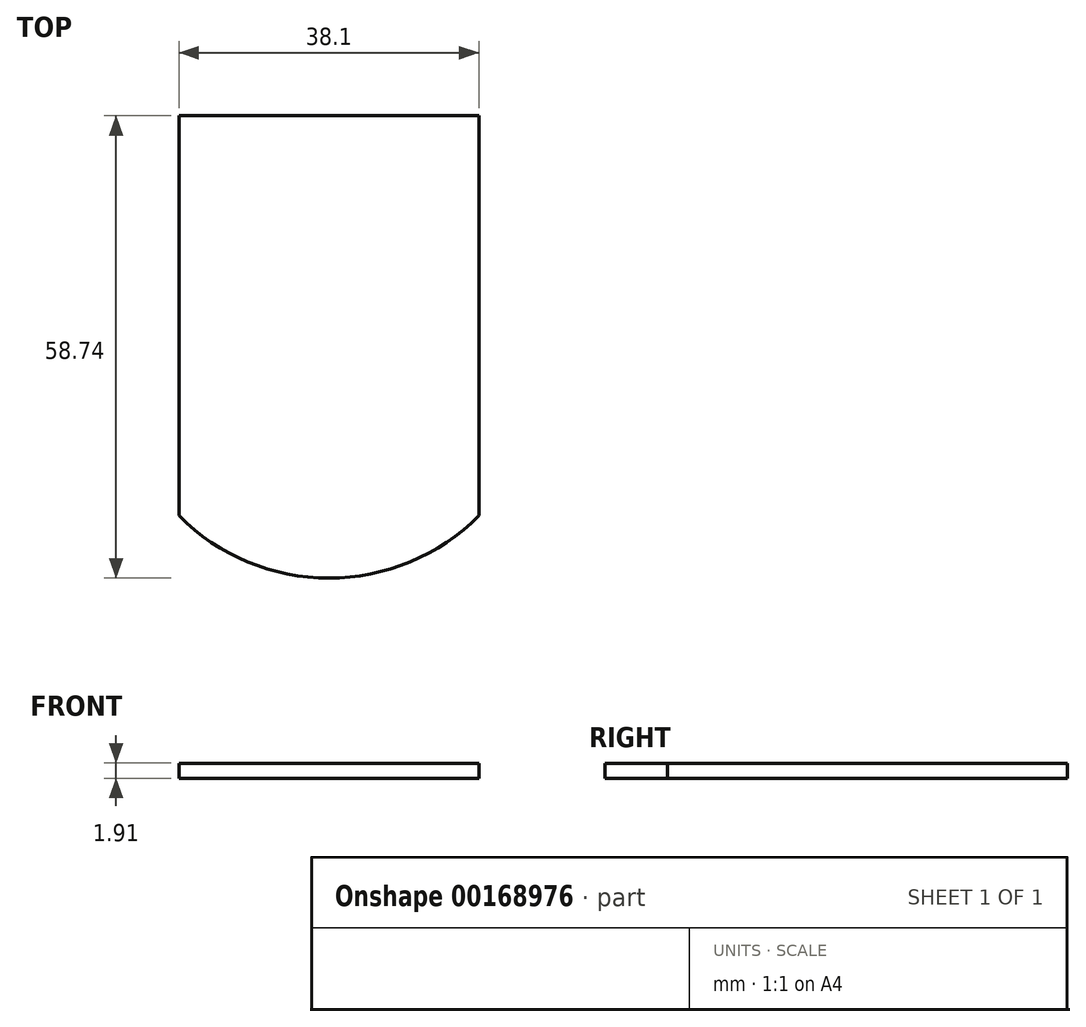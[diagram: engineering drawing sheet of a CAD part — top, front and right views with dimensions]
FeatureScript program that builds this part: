
annotation { "Feature Type Name" : "Feature", "Feature Type Description" : "" }
export const myFeature = defineFeature(function(context is Context, id is Id, definition is map)
    precondition{}
    {
        {
            var Q0;
            Q0=qCreatedBy(makeId("Top.planeOp"),FACE);
            var sketch = newSketch(context, id + "F0", { "sketchPlane" : qUnion([Q0])});
            skLineSegment(sketch, "E0.bottom", {"start": v(19.05, 25.4) * mm, "end": v(-19.05, 25.4) * mm});
            skLineSegment(sketch, "E0.top", {"start": v(19.05, -25.4) * mm, "end": v(-19.05, -25.4) * mm});
            skLineSegment(sketch, "E0.left", {"start": v(19.05, 25.4) * mm, "end": v(19.05, -25.4) * mm});
            skLineSegment(sketch, "E0.right", {"start": v(-19.05, 25.4) * mm, "end": v(-19.05, -25.4) * mm});
            skPoint(sketch, "E0.middle", {"position": v(0, 0) * mm});
            skArc(sketch, "E1", {"start": v(-19.05, -25.4) * mm, "mid": v(0, -33.34) * mm, "end": v(19.05, -25.4) * mm});
            skSolve(sketch);
        }
        {
            var Q0;
            Q0 = qSketchRegion(id + "F0", true);
            extrude(context, id + "F1", {"entities" : qUnion([Q0]), "depth" : 1.9 * mm});
        }
    });
